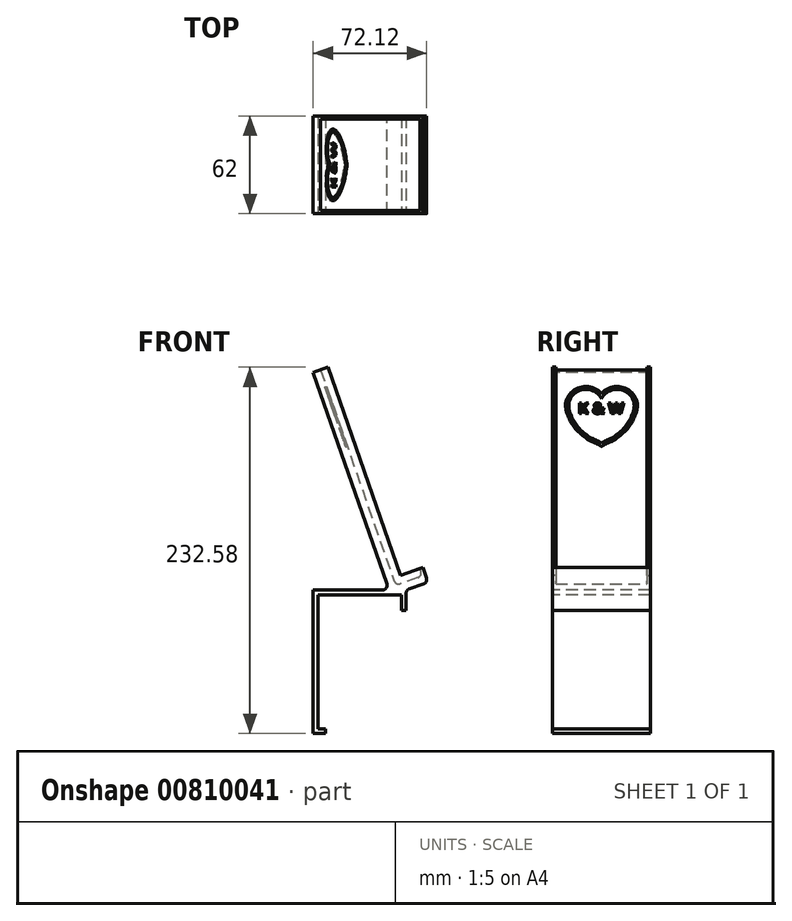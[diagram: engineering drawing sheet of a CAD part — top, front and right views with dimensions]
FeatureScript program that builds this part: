
annotation { "Feature Type Name" : "Feature", "Feature Type Description" : "" }
export const myFeature = defineFeature(function(context is Context, id is Id, definition is map)
    precondition{}
    {
        {
            var Q0;
            Q0=qCreatedBy(makeId("Top.planeOp"),FACE);
            var sketch = newSketch(context, id + "F0", { "sketchPlane" : qUnion([Q0])});
            skLineSegment(sketch, "E0.bottom", {"start": v(-26.5, 31) * mm, "end": v(26.5, 31) * mm});
            skLineSegment(sketch, "E0.top", {"start": v(-26.5, -31) * mm, "end": v(26.5, -31) * mm});
            skLineSegment(sketch, "E0.left", {"start": v(0, 31) * mm, "end": v(0, -31) * mm, "construction": true});
            skLineSegment(sketch, "E0.right", {"start": v(26.5, 31) * mm, "end": v(26.5, -31) * mm});
            skLineSegment(sketch, "E1.MirrorCS", {"start": v(-26.5, 31) * mm, "end": v(-26.5, -31) * mm});
            skSolve(sketch);
        }
        {
            var Q0;
            Q0 = qSketchRegion(id + "F0", true);
            extrude(context, id + "F1", {"entities" : qUnion([Q0]), "depth" : 3 * mm, "offsetDistance" : 25 * mm});
        }
        {
            var Q0;
            Q0=makeQuery(id+"F1.opExtrude","SWEPT_FACE",FACE,{"disambiguationData":[OSD([sQuery(id+"F0.wireOp",EDGE,"E0.top")])]});
            var sketch = newSketch(context, id + "F2", { "sketchPlane" : qUnion([Q0])});
            skLineSegment(sketch, "E2", {"start": v(-26.5, 3) * mm, "end": v(-29.5, 3) * mm});
            skLineSegment(sketch, "E3", {"start": v(-29.5, 3) * mm, "end": v(-29.5, -88) * mm});
            skLineSegment(sketch, "E4", {"start": v(-26.5, -85) * mm, "end": v(-26.5, 3) * mm});
            skLineSegment(sketch, "E5", {"start": v(-29.5, -88) * mm, "end": v(-21.5, -88) * mm});
            skLineSegment(sketch, "E6", {"start": v(-21.5, -88) * mm, "end": v(-21.5, -85) * mm});
            skLineSegment(sketch, "E7", {"start": v(-21.5, -85) * mm, "end": v(-26.5, -85) * mm});
            skLineSegment(sketch, "E8", {"start": v(26.5, 3) * mm, "end": v(29.5, 3) * mm});
            skLineSegment(sketch, "E9", {"start": v(29.5, 3) * mm, "end": v(29.5, -10) * mm});
            skLineSegment(sketch, "E10", {"start": v(29.5, -10) * mm, "end": v(26.5, -10) * mm});
            skLineSegment(sketch, "E11", {"start": v(26.5, -10) * mm, "end": v(26.5, 3) * mm});
            skLineSegment(sketch, "E12", {"start": v(22.91, 6) * mm, "end": v(-24.78, 142.93) * mm});
            skLineSegment(sketch, "E13", {"start": v(-24.78, 142.93) * mm, "end": v(-29.5, 141.29) * mm});
            skLineSegment(sketch, "E14", {"start": v(-29.5, 141.29) * mm, "end": v(18.66, 3) * mm});
            skLineSegment(sketch, "E15", {"start": v(29.5, 3) * mm, "end": v(43.44, 7.86) * mm});
            skLineSegment(sketch, "E16", {"start": v(43.44, 7.86) * mm, "end": v(40.15, 17.3) * mm});
            skLineSegment(sketch, "E17", {"start": v(40.15, 17.3) * mm, "end": v(38.27, 16.64) * mm});
            skLineSegment(sketch, "E18", {"start": v(38.27, 16.64) * mm, "end": v(39.91, 11.92) * mm});
            skLineSegment(sketch, "E19", {"start": v(39.91, 11.92) * mm, "end": v(22.91, 6) * mm});
            skSolve(sketch);
        }
        {
            var Q0;
            Q0 = qSketchRegion(id + "F2", true);
            var Q1;
            {var subQ1=sQuery(id+"F2.wireOp",EDGE,"E8");Q1=makeQuery(id+"F2.imprint","IMPRINT",FACE,{"disambiguationData":[TD([[makeQuery(id+"F2.imprint","IMPRINT",EDGE,{"derivedFrom":subQ1}),1.0]])]});}
            var Q2;
            Q2=makeQuery(id+"F1.opExtrude","SWEPT_FACE",FACE,{"disambiguationData":[OSD([sQuery(id+"F0.wireOp",EDGE,"E0.bottom")])]});
            extrude(context, id + "F3", {"entities" : qUnion([Q0, Q1]), "operationType" : NewBodyOperationType.ADD, "endBound" : BoundingType.UP_TO_SURFACE, "oppositeDirection" : true, "depth" : 25 * mm, "endBoundEntityFace" : qUnion([Q2]), "offsetDistance" : 25 * mm});
        }
        {
            var Q0;
            Q0=makeQuery(id+"F3.opExtrude","SWEPT_FACE",FACE,{"disambiguationData":[OSD([sQuery(id+"F2.wireOp",EDGE,"E12")])]});
            var sketch = newSketch(context, id + "F4", { "sketchPlane" : qUnion([Q0])});
            skLineSegment(sketch, "E20", {"start": v(-31, 143.13) * mm, "end": v(-29, 143.13) * mm});
            skLineSegment(sketch, "E21", {"start": v(-29, 143.13) * mm, "end": v(-29, -1.87) * mm});
            skLineSegment(sketch, "E22", {"start": v(-29, -1.87) * mm, "end": v(-31, -1.87) * mm});
            skLineSegment(sketch, "E23", {"start": v(-31, -1.87) * mm, "end": v(-31, 143.13) * mm});
            skLineSegment(sketch, "E24", {"start": v(0, 143.13) * mm, "end": v(0, -8.04) * mm, "construction": true});
            skLineSegment(sketch, "E25.MirrorCS", {"start": v(29, -1.87) * mm, "end": v(31, -1.87) * mm});
            skLineSegment(sketch, "E26.MirrorCS", {"start": v(31, 143.13) * mm, "end": v(29, 143.13) * mm});
            skLineSegment(sketch, "E27.MirrorCS", {"start": v(31, -1.87) * mm, "end": v(31, 143.13) * mm});
            skLineSegment(sketch, "E28.MirrorCS", {"start": v(29, 143.13) * mm, "end": v(29, -1.87) * mm});
            skSolve(sketch);
        }
        {
            var Q0;
            Q0 = qSketchRegion(id + "F4", true);
            extrude(context, id + "F5", {"entities" : qUnion([Q0]), "operationType" : NewBodyOperationType.ADD, "depth" : 5 * mm, "offsetDistance" : 25 * mm});
        }
        {
            var Q0;
            Q0=makeQuery(id+"F3.opExtrude","SWEPT_EDGE",EDGE,{"disambiguationData":[OSD([sQuery(id+"F2.wireOp",EDGE,"E8"),sQuery(id+"F2.wireOp",EDGE,"E9"),sQuery(id+"F2.wireOp",EDGE,"E15")])]});
            var Q1;
            Q1=makeQuery(id+"F3.opExtrude","SWEPT_EDGE",EDGE,{"disambiguationData":[OSD([sQuery(id+"F2.wireOp",EDGE,"E15"),sQuery(id+"F2.wireOp",EDGE,"E16")])]});
            var Q2;
            Q2=makeQuery(id+"F3.opExtrude","SWEPT_EDGE",EDGE,{"disambiguationData":[OSD([sQuery(id+"F2.wireOp",EDGE,"E18"),sQuery(id+"F2.wireOp",EDGE,"E19")])]});
            var Q3;
            Q3=makeQuery(id+"F5.opExtrude","CAP_EDGE",EDGE,{"disambiguationData":[OSD([sQuery(id+"F4.wireOp",EDGE,"E28.MirrorCS")])],"isStart":true});
            var Q4;
            Q4=makeQuery(id+"F5.opExtrude","CAP_EDGE",EDGE,{"disambiguationData":[OSD([sQuery(id+"F4.wireOp",EDGE,"E21")])],"isStart":true});
            var Q5;
            Q5=makeQuery(id+"F3.opExtrude","SWEPT_EDGE",EDGE,{"disambiguationData":[OSD([sQuery(id+"F0.wireOp",EDGE,"E0.top"),sQuery(id+"F2.wireOp",EDGE,"E14")])]});
            fillet(context, id + "F6", {"entities" : qUnion([Q0, Q1, Q2, Q3, Q4, Q5]), "radius" : 3 * mm, "tangentPropagation" : true, "allowEdgeOverflow" : false});
        }
        {
            var Q0;
            {var subQ0=sQuery(id+"F0.wireOp",EDGE,"E0.top");Q0=makeQuery(id+"F5.boolean.opBoolean","MERGE",FACE,{"derivedFrom":[makeQuery(id+"F3.boolean.opBoolean","MERGE",FACE,{"derivedFrom":[makeQuery(id+"F1.opExtrude","SWEPT_FACE",FACE,{"disambiguationData":[OSD([subQ0])]}),makeQuery(id+"F3.opExtrude","CAP_FACE",FACE,{"disambiguationData":[OSD([sQuery(id+"F2.wireOp",EDGE,"E2"),sQuery(id+"F2.wireOp",EDGE,"E3"),sQuery(id+"F2.wireOp",EDGE,"E4"),sQuery(id+"F2.wireOp",EDGE,"E5"),sQuery(id+"F2.wireOp",EDGE,"E6"),sQuery(id+"F2.wireOp",EDGE,"E7")])],"isStart":true}),makeQuery(id+"F3.opExtrude","CAP_FACE",FACE,{"disambiguationData":[OSD([subQ0,sQuery(id+"F2.wireOp",EDGE,"E9"),sQuery(id+"F2.wireOp",EDGE,"E10"),sQuery(id+"F2.wireOp",EDGE,"E11"),sQuery(id+"F2.wireOp",EDGE,"E12"),sQuery(id+"F2.wireOp",EDGE,"E13"),sQuery(id+"F2.wireOp",EDGE,"E14"),sQuery(id+"F2.wireOp",EDGE,"E15"),sQuery(id+"F2.wireOp",EDGE,"E16"),sQuery(id+"F2.wireOp",EDGE,"E17"),sQuery(id+"F2.wireOp",EDGE,"E18"),sQuery(id+"F2.wireOp",EDGE,"E19")])],"isStart":true})]}),makeQuery(id+"F5.opExtrude","SWEPT_FACE",FACE,{"disambiguationData":[OSD([sQuery(id+"F4.wireOp",EDGE,"E23")])]})]});}
            var sketch = newSketch(context, id + "F7", { "sketchPlane" : qUnion([Q0])});
            skLineSegment(sketch, "E29", {"start": v(27.63, 7.64) * mm, "end": v(37.08, 10.93) * mm});
            skLineSegment(sketch, "E30", {"start": v(38.92, 14.75) * mm, "end": v(38.27, 16.64) * mm});
            skLineSegment(sketch, "E31", {"start": v(38.27, 16.64) * mm, "end": v(25.99, 12.37) * mm});
            skLineSegment(sketch, "E32", {"start": v(25.99, 12.37) * mm, "end": v(27.63, 7.64) * mm});
            skArc(sketch, "E33", {"start": v(37.08, 10.93) * mm, "mid": v(38.8, 12.46) * mm, "end": v(38.92, 14.75) * mm});
            skSolve(sketch);
        }
        {
            var Q0;
            Q0 = qSketchRegion(id + "F7", true);
            var Q1;
            Q1=makeQuery(id+"F5.opExtrude","SWEPT_FACE",FACE,{"disambiguationData":[OSD([sQuery(id+"F4.wireOp",EDGE,"E21")])]});
            extrude(context, id + "F8", {"entities" : qUnion([Q0]), "operationType" : NewBodyOperationType.ADD, "endBound" : BoundingType.UP_TO_SURFACE, "oppositeDirection" : true, "depth" : 25 * mm, "endBoundEntityFace" : qUnion([Q1]), "offsetDistance" : 25 * mm});
        }
        {
            var Q0;
            {var subQ0=sQuery(id+"F0.wireOp",EDGE,"E0.bottom");Q0=makeQuery(id+"F5.boolean.opBoolean","MERGE",FACE,{"derivedFrom":[makeQuery(id+"F3.boolean.opBoolean","MERGE",FACE,{"derivedFrom":[makeQuery(id+"F1.opExtrude","SWEPT_FACE",FACE,{"disambiguationData":[OSD([subQ0])]}),makeQuery(id+"F3.opExtrude","CAP_FACE",FACE,{"disambiguationData":[OSD([subQ0]),OD(0.0)],"isStart":false}),makeQuery(id+"F3.opExtrude","CAP_FACE",FACE,{"disambiguationData":[OSD([subQ0]),OD(1.0)],"isStart":false})]}),makeQuery(id+"F5.opExtrude","SWEPT_FACE",FACE,{"disambiguationData":[OSD([sQuery(id+"F4.wireOp",EDGE,"E27.MirrorCS")])]})]});}
            var sketch = newSketch(context, id + "F9", { "sketchPlane" : qUnion([Q0])});
            skLineSegment(sketch, "E34", {"start": v(-27.63, 7.64) * mm, "end": v(-37.08, 10.93) * mm});
            skLineSegment(sketch, "E35", {"start": v(-38.92, 14.75) * mm, "end": v(-38.27, 16.64) * mm});
            skLineSegment(sketch, "E36", {"start": v(-38.27, 16.64) * mm, "end": v(-25.99, 12.37) * mm});
            skLineSegment(sketch, "E37", {"start": v(-25.99, 12.37) * mm, "end": v(-27.63, 7.64) * mm});
            skArc(sketch, "E38", {"start": v(-38.92, 14.75) * mm, "mid": v(-38.8, 12.46) * mm, "end": v(-37.08, 10.93) * mm});
            skSolve(sketch);
        }
        {
            var Q0;
            Q0 = qSketchRegion(id + "F9", true);
            var Q1;
            Q1=makeQuery(id+"F5.opExtrude","SWEPT_FACE",FACE,{"disambiguationData":[OSD([sQuery(id+"F4.wireOp",EDGE,"E28.MirrorCS")])]});
            extrude(context, id + "F10", {"entities" : qUnion([Q0]), "operationType" : NewBodyOperationType.ADD, "endBound" : BoundingType.UP_TO_SURFACE, "oppositeDirection" : true, "depth" : 25 * mm, "endBoundEntityFace" : qUnion([Q1]), "offsetDistance" : 25 * mm});
        }
        {
            var Q0;
            Q0=makeQuery(id+"F3.opExtrude","SWEPT_EDGE",EDGE,{"disambiguationData":[OSD([sQuery(id+"F2.wireOp",EDGE,"E12"),sQuery(id+"F2.wireOp",EDGE,"E19")])]});
            fillet(context, id + "F11", {"entities" : qUnion([Q0]), "radius" : 3 * mm, "tangentPropagation" : true, "allowEdgeOverflow" : false});
        }
        {
            var Q0;
            Q0=makeQuery(id+"F3.opExtrude","SWEPT_FACE",FACE,{"disambiguationData":[OSD([sQuery(id+"F2.wireOp",EDGE,"E12")])]});
            var sketch = newSketch(context, id + "F12", { "sketchPlane" : qUnion([Q0])});
            skText(sketch, "E39", { "text": "K & W", "fontName": "OpenSans-Bold.ttf"});
            skLineSegment(sketch, "E40", {"start": v(0, -2.78) * mm, "end": v(0, 113.63) * mm, "construction": true});
            skArc(sketch, "E41", {"start": v(0, 127.38) * mm, "mid": v(-15.64, 130.58) * mm, "end": v(-22.48, 116.16) * mm});
            skArc(sketch, "E42", {"start": v(-22.48, 116.16) * mm, "mid": v(-15.97, 102.88) * mm, "end": v(-4.19, 93.94) * mm});
            skArc(sketch, "E43", {"start": v(0, 91.52) * mm, "mid": v(-2.03, 92.85) * mm, "end": v(-4.19, 93.94) * mm});
            skArc(sketch, "E44.MirrorCS", {"start": v(0, 127.38) * mm, "mid": v(15.64, 130.58) * mm, "end": v(22.48, 116.16) * mm});
            skArc(sketch, "E45.MirrorCS", {"start": v(22.48, 116.16) * mm, "mid": v(15.97, 102.88) * mm, "end": v(4.19, 93.94) * mm});
            skArc(sketch, "E46.MirrorCS", {"start": v(0, 91.52) * mm, "mid": v(2.03, 92.85) * mm, "end": v(4.19, 93.94) * mm});
            skArc(sketch, "E47.0", {"start": v(0, 123.74) * mm, "mid": v(13.45, 129.34) * mm, "end": v(20.52, 116.6) * mm});
            skArc(sketch, "E47.1", {"start": v(-20.52, 116.6) * mm, "mid": v(-14.43, 104.15) * mm, "end": v(-3.38, 95.77) * mm});
            skArc(sketch, "E47.2", {"start": v(0, 93.95) * mm, "mid": v(-1.65, 94.93) * mm, "end": v(-3.38, 95.77) * mm});
            skArc(sketch, "E47.3", {"start": v(0, 123.74) * mm, "mid": v(-13.45, 129.34) * mm, "end": v(-20.52, 116.6) * mm});
            skArc(sketch, "E47.4", {"start": v(0, 93.95) * mm, "mid": v(1.65, 94.93) * mm, "end": v(3.38, 95.77) * mm});
            skArc(sketch, "E47.5", {"start": v(20.52, 116.6) * mm, "mid": v(14.43, 104.15) * mm, "end": v(3.38, 95.77) * mm});
            const initialGuessF12  = {"E39": [-0.015, 0.11363, 1, 0, 0.00728]};
            skSetInitialGuess(sketch, initialGuessF12);
            skSolve(sketch);
        }
        {
            var Q0;
            Q0=makeQuery(id+"F12.imprint","IMPRINT",FACE,{"disambiguationData":[TD([[makeQuery(id+"F12.imprint","IMPRINT",EDGE,{"derivedFrom":sQuery(id+"F12.wireOp",EDGE,"E41")}),1.0]])]});
            var Q1;
            Q1=makeQuery(id+"F12.imprint","IMPRINT",FACE,{"disambiguationData":[TD([[makeQuery(id+"F12.imprint","IMPRINT",EDGE,{"derivedFrom":sQuery(id+"F12.wireOp",EDGE,"E39.sketch_text.stroke-0")}),-1.0]])]});
            var Q2;
            Q2=makeQuery(id+"F12.imprint","IMPRINT",FACE,{"disambiguationData":[TD([[makeQuery(id+"F12.imprint","IMPRINT",EDGE,{"derivedFrom":sQuery(id+"F12.wireOp",EDGE,"E39.sketch_text.stroke-13")}),-1.0]])]});
            var Q3;
            Q3=makeQuery(id+"F12.imprint","IMPRINT",FACE,{"disambiguationData":[TD([[makeQuery(id+"F12.imprint","IMPRINT",EDGE,{"derivedFrom":sQuery(id+"F12.wireOp",EDGE,"E39.sketch_text.stroke-47")}),-1.0]])]});
            extrude(context, id + "F13", {"entities" : qUnion([Q0, Q1, Q2, Q3]), "operationType" : NewBodyOperationType.REMOVE, "oppositeDirection" : true, "depth" : 1 * mm, "offsetDistance" : 25 * mm});
        }
    });
